# Revit family: HL_Сифон с уплотнением_HL136NT
name_source: partatom
category: Příslušenství trubek
revit_build: Autodesk Revit 2016 (Build: 20161004_0715(x64)
units: mm (PartAtom-declared; Revit-internal decimal feet)

## family parameters
Kóta kulaté spojky = Použít průměr
Nadpis OmniClass = General Pipework and Ductwork Products
Ořezat dutým tvarem při načtení = Ne
Sdílené = Ne
Typ součásti = Normální
Vždy vertikální = Ano
Založené na pracovní rovině = Ne
Číslo OmniClass = 23.60.30.00

## types (1)
- HL_Сифон с уплотнением_HL136NT
    Cena = 0 $
    EAN = 9003076036288
    Komentáře k typům = Прозрачный сифон для кондиционеров с гидрозатвором и запахозапирающим устройством DN40, обжимное соединение DN32 или гладкие штуцеры 12 -18 мм, горизонтальное или вертикальное соединение, механическое запахозапирающее устройство, прочистка-грязесборник.
    Model = HL136NT
    Popis = Кондиционирование и Вентиляция
    URL = http://www.hutterer-lechner.com
    Výrobce = HL Hutterer & Lechner GmbH
    ВЕС = 0,23 kg
    ВЫСОТА МОНТАЖА = 95 mm
    МАТЕРИАЛ = PP transparent
    НОМИНАЛЬНЫЙ ДИАМЕТР 2 = 40 mm
    ПРОИЗВОДИТЕЛЬНОСТЬ = 0,37 l/s
    ПРОПУСКНАЯ СПОСОБНОСТЬ = 0.0 m³/h
    РАЗМЕР = DN40 x 5/4" bzw. d 12-18mm
    материал = Plactic - Transparent
    материал 2 = Plactic - Black
